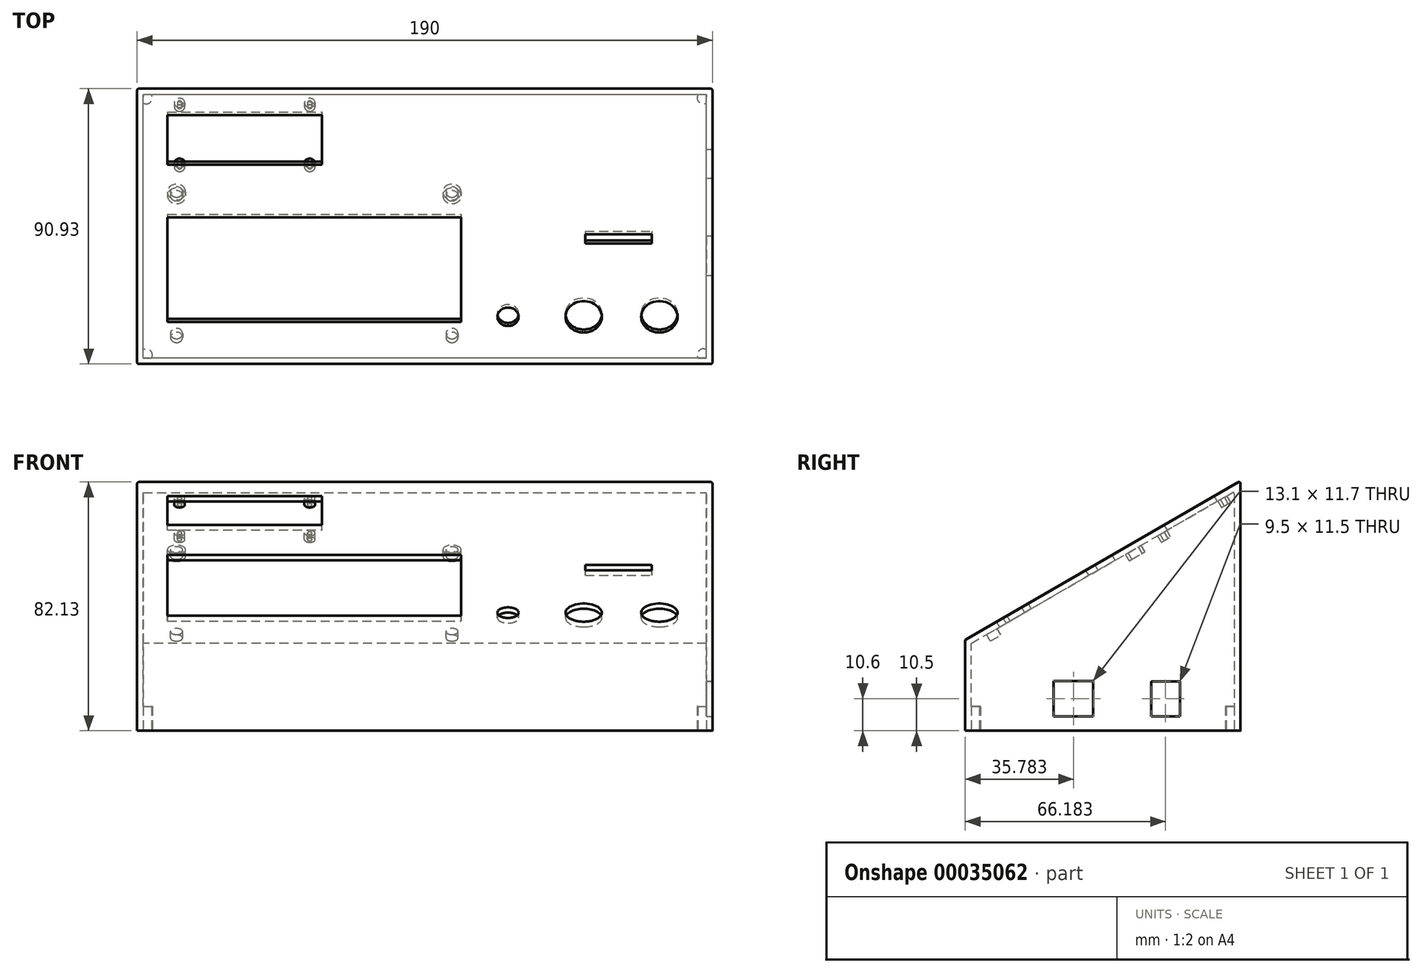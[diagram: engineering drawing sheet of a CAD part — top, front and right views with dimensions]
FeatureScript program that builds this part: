
annotation { "Feature Type Name" : "Feature", "Feature Type Description" : "" }
export const myFeature = defineFeature(function(context is Context, id is Id, definition is map)
    precondition{}
    {
        {
            var Q0;
            Q0=qCreatedBy(makeId("Right.planeOp"),FACE);
            var sketch = newSketch(context, id + "F0", { "sketchPlane" : qUnion([Q0])});
            skLineSegment(sketch, "E0", {"start": v(0, 0) * mm, "end": v(0, 30) * mm});
            skLineSegment(sketch, "E1", {"start": v(0, 30) * mm, "end": v(90.93, 82.5) * mm});
            skLineSegment(sketch, "E2", {"start": v(90.93, 82.5) * mm, "end": v(90.93, 0) * mm});
            skLineSegment(sketch, "E3", {"start": v(0, 0) * mm, "end": v(90.93, 0) * mm});
            skSolve(sketch);
        }
        {
            var Q0;
            Q0 = qSketchRegion(id + "F0", true);
            extrude(context, id + "F1", {"entities" : qUnion([Q0]), "depth" : 190 * mm});
        }
        {
            var Q0;
            Q0=makeQuery(id+"F1.opExtrude","SWEPT_FACE",FACE,{"disambiguationData":[OSD([sQuery(id+"F0.wireOp",EDGE,"E3")])]});
            shell(context, id + "F2", {"entities" : qUnion([Q0]), "thickness" : 2 * mm});
        }
        {
            var Q0;
            Q0=makeQuery(id+"F1.opExtrude","SWEPT_FACE",FACE,{"disambiguationData":[OSD([sQuery(id+"F0.wireOp",EDGE,"E1")])]});
            var sketch = newSketch(context, id + "F3", { "sketchPlane" : qUnion([Q0])});
            skLineSegment(sketch, "E4.bottom", {"start": v(10, 110) * mm, "end": v(61, 110) * mm});
            skLineSegment(sketch, "E4.top", {"start": v(10, 91) * mm, "end": v(61, 91) * mm});
            skLineSegment(sketch, "E4.left", {"start": v(10, 110) * mm, "end": v(10, 91) * mm});
            skLineSegment(sketch, "E4.right", {"start": v(61, 110) * mm, "end": v(61, 91) * mm});
            skLineSegment(sketch, "E5.bottom", {"start": v(10, 71) * mm, "end": v(107, 71) * mm});
            skLineSegment(sketch, "E5.top", {"start": v(10, 31) * mm, "end": v(107, 31) * mm});
            skLineSegment(sketch, "E5.left", {"start": v(10, 71) * mm, "end": v(10, 31) * mm});
            skLineSegment(sketch, "E5.right", {"start": v(107, 71) * mm, "end": v(107, 31) * mm});
            skSolve(sketch);
        }
        {
            var Q0;
            Q0=makeQuery(id+"F3.imprint","IMPRINT",FACE,{"disambiguationData":[TD([[makeQuery(id+"F3.imprint","IMPRINT",EDGE,{"derivedFrom":sQuery(id+"F3.wireOp",EDGE,"E4.bottom")}),-1.0]])]});
            var Q1;
            Q1=makeQuery(id+"F3.imprint","IMPRINT",FACE,{"disambiguationData":[TD([[makeQuery(id+"F3.imprint","IMPRINT",EDGE,{"derivedFrom":sQuery(id+"F3.wireOp",EDGE,"E5.bottom")}),-1.0]])]});
            var Q2;
            Q2=sQuery(id+"F3.wireOp",EDGE,"E5.top");
            extrude(context, id + "F4", {"entities" : qUnion([Q0, Q1]), "operationType" : NewBodyOperationType.REMOVE, "surfaceEntities" : qUnion([Q2]), "oppositeDirection" : true, "depth" : 2 * mm});
        }
        {
            var Q0;
            Q0=makeQuery(id+"F1.opExtrude","SWEPT_FACE",FACE,{"disambiguationData":[OSD([sQuery(id+"F0.wireOp",EDGE,"E1")])]});
            var sketch = newSketch(context, id + "F5", { "sketchPlane" : qUnion([Q0])});
            skCircle(sketch, "E6", {"center": v(122.5, 33) * mm, "radius": 3.5 * mm});
            skCircle(sketch, "E7", {"center": v(147.5, 33) * mm, "radius": 6 * mm});
            skCircle(sketch, "E8", {"center": v(172.5, 33) * mm, "radius": 6 * mm});
            skCircle(sketch, "E9", {"center": v(172.5, 33) * mm, "radius": 8.5 * mm, "construction": true});
            skSolve(sketch);
        }
        {
            var Q0;
            Q0 = qSketchRegion(id + "F5", true);
            extrude(context, id + "F6", {"entities" : qUnion([Q0]), "operationType" : NewBodyOperationType.REMOVE, "oppositeDirection" : true, "depth" : 2 * mm});
        }
        {
            var Q0;
            Q0=makeQuery(id+"F1.opExtrude","CAP_FACE",FACE,{"disambiguationData":[OSD([sQuery(id+"F0.wireOp",EDGE,"E0"),sQuery(id+"F0.wireOp",EDGE,"E1"),sQuery(id+"F0.wireOp",EDGE,"E2"),sQuery(id+"F0.wireOp",EDGE,"E3")])],"isStart":false});
            var sketch = newSketch(context, id + "F7", { "sketchPlane" : qUnion([Q0])});
            skLineSegment(sketch, "E10.bottom", {"start": v(61.43, 16.25) * mm, "end": v(70.93, 16.25) * mm});
            skLineSegment(sketch, "E10.top", {"start": v(61.43, 4.75) * mm, "end": v(70.93, 4.75) * mm});
            skLineSegment(sketch, "E10.left", {"start": v(61.43, 16.25) * mm, "end": v(61.43, 4.75) * mm});
            skLineSegment(sketch, "E10.right", {"start": v(70.93, 16.25) * mm, "end": v(70.93, 4.75) * mm});
            skLineSegment(sketch, "E11.bottom", {"start": v(42.33, 4.75) * mm, "end": v(29.23, 4.75) * mm});
            skLineSegment(sketch, "E11.top", {"start": v(42.33, 16.45) * mm, "end": v(29.23, 16.45) * mm});
            skLineSegment(sketch, "E11.left", {"start": v(42.33, 4.75) * mm, "end": v(42.33, 16.45) * mm});
            skLineSegment(sketch, "E11.right", {"start": v(29.23, 4.75) * mm, "end": v(29.23, 16.45) * mm});
            skSolve(sketch);
        }
        {
            var Q0;
            Q0 = qSketchRegion(id + "F7", true);
            extrude(context, id + "F8", {"entities" : qUnion([Q0]), "operationType" : NewBodyOperationType.REMOVE, "oppositeDirection" : true, "depth" : 2 * mm});
        }
        {
            var Q0;
            Q0=makeQuery(id+"F1.opExtrude","SWEPT_FACE",FACE,{"disambiguationData":[OSD([sQuery(id+"F0.wireOp",EDGE,"E1")])]});
            var sketch = newSketch(context, id + "F9", { "sketchPlane" : qUnion([Q0])});
            skLineSegment(sketch, "E12.bottom", {"start": v(139, 110) * mm, "end": v(180, 110) * mm, "construction": true});
            skLineSegment(sketch, "E12.top", {"start": v(139, 58) * mm, "end": v(180, 58) * mm, "construction": true});
            skLineSegment(sketch, "E12.left", {"start": v(139, 110) * mm, "end": v(139, 58) * mm, "construction": true});
            skLineSegment(sketch, "E12.right", {"start": v(180, 110) * mm, "end": v(180, 58) * mm, "construction": true});
            skLineSegment(sketch, "E13.bottom", {"start": v(148, 64.5) * mm, "end": v(170, 64.5) * mm});
            skLineSegment(sketch, "E13.top", {"start": v(148, 61) * mm, "end": v(170, 61) * mm});
            skLineSegment(sketch, "E13.left", {"start": v(148, 64.5) * mm, "end": v(148, 61) * mm});
            skLineSegment(sketch, "E13.right", {"start": v(170, 64.5) * mm, "end": v(170, 61) * mm});
            skSolve(sketch);
        }
        {
            var Q0;
            Q0=makeQuery(id+"F9.imprint","IMPRINT",FACE,{"disambiguationData":[TD([[makeQuery(id+"F9.imprint","IMPRINT",EDGE,{"derivedFrom":sQuery(id+"F9.wireOp",EDGE,"E13.bottom")}),-1.0]])]});
            var Q1;
            Q1=sQuery(id+"F9.wireOp",EDGE,"E13.top");
            extrude(context, id + "F10", {"entities" : qUnion([Q0]), "operationType" : NewBodyOperationType.REMOVE, "surfaceEntities" : qUnion([Q1]), "oppositeDirection" : true, "depth" : 2 * mm});
        }
        {
            var Q0;
            Q0=makeQuery(id+"F1.opExtrude","SWEPT_FACE",FACE,{"disambiguationData":[OSD([sQuery(id+"F0.wireOp",EDGE,"E1")])]});
            var sketch = newSketch(context, id + "F11", { "sketchPlane" : qUnion([Q0])});
            skCircle(sketch, "E14", {"center": v(57, 112) * mm, "radius": 0.75 * mm});
            skCircle(sketch, "E15", {"center": v(14, 112) * mm, "radius": 0.75 * mm});
            skCircle(sketch, "E16", {"center": v(14, 89) * mm, "radius": 0.75 * mm});
            skCircle(sketch, "E17", {"center": v(57, 89) * mm, "radius": 0.75 * mm});
            skCircle(sketch, "E18.0", {"center": v(14, 89) * mm, "radius": 1.75 * mm});
            skCircle(sketch, "E19.0", {"center": v(14, 112) * mm, "radius": 1.75 * mm});
            skLineSegment(sketch, "E20.0", {"start": v(5, 115) * mm, "end": v(5, 20) * mm});
            skLineSegment(sketch, "E20.1", {"start": v(185, 115) * mm, "end": v(5, 115) * mm});
            skLineSegment(sketch, "E20.2", {"start": v(185, 20) * mm, "end": v(185, 115) * mm});
            skLineSegment(sketch, "E20.3", {"start": v(5, 20) * mm, "end": v(185, 20) * mm});
            skCircle(sketch, "E21.0", {"center": v(57, 112) * mm, "radius": 1.75 * mm});
            skCircle(sketch, "E22.0", {"center": v(57, 89) * mm, "radius": 1.75 * mm});
            skSolve(sketch);
        }
        {
            var Q0;
            Q0=makeQuery(id+"F11.imprint","IMPRINT",FACE,{"disambiguationData":[TD([[makeQuery(id+"F11.imprint","IMPRINT",EDGE,{"derivedFrom":sQuery(id+"F11.wireOp",EDGE,"E15")}),-1.0]])]});
            var Q1;
            Q1=makeQuery(id+"F11.imprint","IMPRINT",FACE,{"disambiguationData":[TD([[makeQuery(id+"F11.imprint","IMPRINT",EDGE,{"derivedFrom":sQuery(id+"F11.wireOp",EDGE,"E16")}),-1.0]])]});
            var Q2;
            Q2=makeQuery(id+"F11.imprint","IMPRINT",FACE,{"disambiguationData":[TD([[makeQuery(id+"F11.imprint","IMPRINT",EDGE,{"derivedFrom":sQuery(id+"F11.wireOp",EDGE,"E14")}),-1.0]])]});
            var Q3;
            Q3=makeQuery(id+"F11.imprint","IMPRINT",FACE,{"disambiguationData":[TD([[makeQuery(id+"F11.imprint","IMPRINT",EDGE,{"derivedFrom":sQuery(id+"F11.wireOp",EDGE,"E17")}),-1.0]])]});
            extrude(context, id + "F12", {"entities" : qUnion([Q0, Q1, Q2, Q3]), "operationType" : NewBodyOperationType.ADD, "oppositeDirection" : true, "depth" : 4.5 * mm});
        }
        {
            var Q0;
            Q0=makeQuery(id+"F1.opExtrude","SWEPT_FACE",FACE,{"disambiguationData":[OSD([sQuery(id+"F0.wireOp",EDGE,"E1")])]});
            var sketch = newSketch(context, id + "F13", { "sketchPlane" : qUnion([Q0])});
            skLineSegment(sketch, "E23.bottom", {"start": v(10, 81) * mm, "end": v(107, 81) * mm, "construction": true});
            skLineSegment(sketch, "E23.top", {"start": v(10, 21) * mm, "end": v(107, 21) * mm, "construction": true});
            skLineSegment(sketch, "E23.left", {"start": v(10, 81) * mm, "end": v(10, 21) * mm, "construction": true});
            skLineSegment(sketch, "E23.right", {"start": v(107, 81) * mm, "end": v(107, 21) * mm, "construction": true});
            skCircle(sketch, "E24", {"center": v(13, 78) * mm, "radius": 2 * mm});
            skCircle(sketch, "E25", {"center": v(104, 78) * mm, "radius": 2 * mm});
            skLineSegment(sketch, "E26", {"start": v(10, 51) * mm, "end": v(107, 51) * mm, "construction": true});
            skCircle(sketch, "E27.MirrorC", {"center": v(13, 24) * mm, "radius": 2 * mm});
            skCircle(sketch, "E28.MirrorC", {"center": v(104, 24) * mm, "radius": 2 * mm});
            skCircle(sketch, "E29", {"center": v(13, 78) * mm, "radius": 3 * mm});
            skCircle(sketch, "E30", {"center": v(104, 78) * mm, "radius": 3 * mm});
            skCircle(sketch, "E31.MirrorC", {"center": v(13, 24) * mm, "radius": 3 * mm});
            skCircle(sketch, "E32.MirrorC", {"center": v(104, 24) * mm, "radius": 3 * mm});
            skSolve(sketch);
        }
        {
            var Q0;
            Q0=makeQuery(id+"F13.imprint","IMPRINT",FACE,{"disambiguationData":[TD([[makeQuery(id+"F13.imprint","IMPRINT",EDGE,{"derivedFrom":sQuery(id+"F13.wireOp",EDGE,"E24")}),-1.0]])]});
            var Q1;
            Q1=makeQuery(id+"F13.imprint","IMPRINT",FACE,{"disambiguationData":[TD([[makeQuery(id+"F13.imprint","IMPRINT",EDGE,{"derivedFrom":sQuery(id+"F13.wireOp",EDGE,"E25")}),-1.0]])]});
            var Q2;
            Q2=makeQuery(id+"F13.imprint","IMPRINT",FACE,{"disambiguationData":[TD([[makeQuery(id+"F13.imprint","IMPRINT",EDGE,{"derivedFrom":sQuery(id+"F13.wireOp",EDGE,"E28.MirrorC")}),1.0]])]});
            var Q3;
            Q3=makeQuery(id+"F13.imprint","IMPRINT",FACE,{"disambiguationData":[TD([[makeQuery(id+"F13.imprint","IMPRINT",EDGE,{"derivedFrom":sQuery(id+"F13.wireOp",EDGE,"E27.MirrorC")}),1.0]])]});
            extrude(context, id + "F14", {"entities" : qUnion([Q0, Q1, Q2, Q3]), "operationType" : NewBodyOperationType.ADD, "oppositeDirection" : true, "depth" : 4.5 * mm});
        }
        {
            var Q0;
            Q0=makeQuery(id+"F1.opExtrude","SWEPT_FACE",FACE,{"disambiguationData":[OSD([sQuery(id+"F0.wireOp",EDGE,"E3")])]});
            var sketch = newSketch(context, id + "F15", { "sketchPlane" : qUnion([Q0])});
            skCircle(sketch, "E33", {"center": v(3, -3) * mm, "radius": 2 * mm});
            skCircle(sketch, "E34", {"center": v(3, -87.93) * mm, "radius": 2 * mm});
            skCircle(sketch, "E35", {"center": v(187, -3) * mm, "radius": 2 * mm});
            skCircle(sketch, "E36", {"center": v(187, -87.93) * mm, "radius": 2 * mm});
            skSolve(sketch);
        }
        {
            var Q0;
            Q0 = qSketchRegion(id + "F15", true);
            extrude(context, id + "F16", {"entities" : qUnion([Q0]), "operationType" : NewBodyOperationType.ADD, "oppositeDirection" : true, "depth" : 8 * mm});
        }
        {
            var Q0;
            Q0=makeQuery(id+"F1.opExtrude","CAP_EDGE",EDGE,{"disambiguationData":[OSD([sQuery(id+"F0.wireOp",EDGE,"E1")])],"isStart":false});
            var Q1;
            Q1=makeQuery(id+"F1.opExtrude","CAP_EDGE",EDGE,{"disambiguationData":[OSD([sQuery(id+"F0.wireOp",EDGE,"E1")])],"isStart":true});
            var Q2;
            Q2=makeQuery(id+"F1.opExtrude","SWEPT_EDGE",EDGE,{"disambiguationData":[OSD([sQuery(id+"F0.wireOp",EDGE,"E0"),sQuery(id+"F0.wireOp",EDGE,"E1")])]});
            var Q3;
            Q3=makeQuery(id+"F1.opExtrude","CAP_EDGE",EDGE,{"disambiguationData":[OSD([sQuery(id+"F0.wireOp",EDGE,"E0")])],"isStart":true});
            var Q4;
            Q4=makeQuery(id+"F1.opExtrude","CAP_EDGE",EDGE,{"disambiguationData":[OSD([sQuery(id+"F0.wireOp",EDGE,"E2")])],"isStart":false});
            var Q5;
            Q5=makeQuery(id+"F1.opExtrude","CAP_EDGE",EDGE,{"disambiguationData":[OSD([sQuery(id+"F0.wireOp",EDGE,"E2")])],"isStart":true});
            var Q6;
            Q6=makeQuery(id+"F1.opExtrude","SWEPT_EDGE",EDGE,{"disambiguationData":[OSD([sQuery(id+"F0.wireOp",EDGE,"E1"),sQuery(id+"F0.wireOp",EDGE,"E2")])]});
            var Q7;
            Q7=makeQuery(id+"F2.opShell","OFFSET_EDGE",EDGE,{"disambiguationData":[OSD([sQuery(id+"F0.wireOp",EDGE,"E1"),sQuery(id+"F0.wireOp",EDGE,"E2")])]});
            var Q8;
            Q8=makeQuery(id+"F1.opExtrude","CAP_EDGE",EDGE,{"disambiguationData":[OSD([sQuery(id+"F0.wireOp",EDGE,"E0")])],"isStart":false});
            fillet(context, id + "F17", {"entities" : qUnion([Q0, Q1, Q2, Q3, Q4, Q5, Q6, Q7, Q8]), "radius" : 0.5 * mm, "tangentPropagation" : true, "allowEdgeOverflow" : false});
        }
    });
